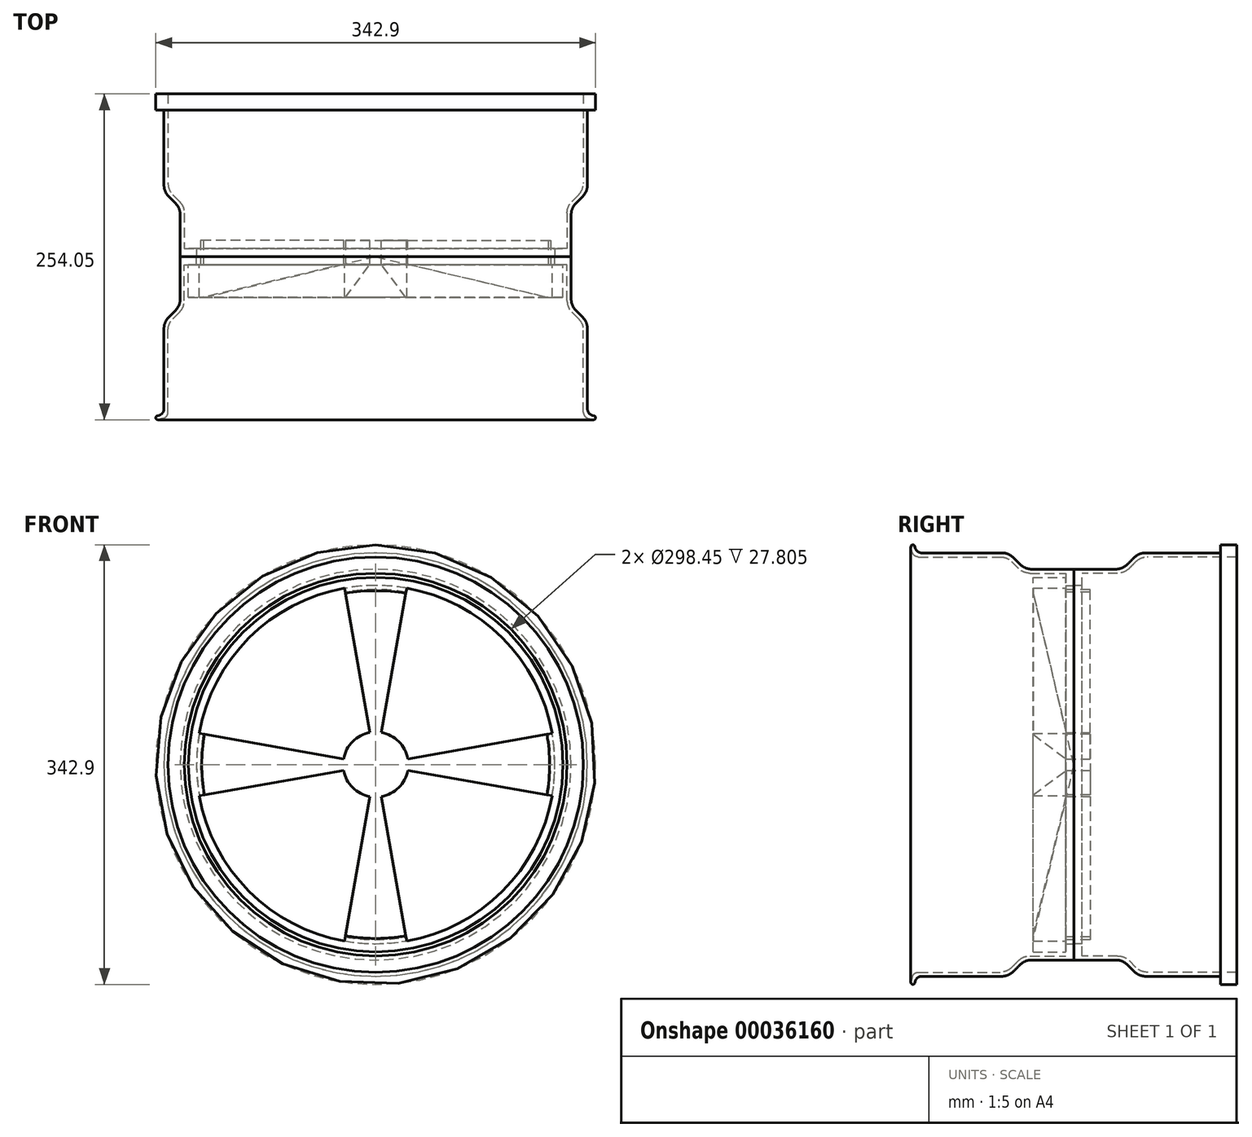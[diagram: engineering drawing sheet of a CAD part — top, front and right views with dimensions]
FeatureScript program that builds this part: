
annotation { "Feature Type Name" : "Feature", "Feature Type Description" : "" }
export const myFeature = defineFeature(function(context is Context, id is Id, definition is map)
    precondition{}
    {
        {
            var Q0;
            Q0=qCreatedBy(makeId("Right.planeOp"),FACE);
            var sketch = newSketch(context, id + "F0", { "sketchPlane" : qUnion([Q0])});
            skLineSegment(sketch, "E0", {"start": v(-127, 169.45) * mm, "end": v(-124.98, 161.93) * mm});
            skLineSegment(sketch, "E1", {"start": v(-39.42, 149.22) * mm, "end": v(-6.35, 149.22) * mm});
            skLineSegment(sketch, "E2", {"start": v(-6.35, 149.22) * mm, "end": v(-6.35, 139.7) * mm});
            skLineSegment(sketch, "E3", {"start": v(-6.35, 139.7) * mm, "end": v(0, 139.7) * mm});
            skLineSegment(sketch, "E4", {"start": v(0, 139.7) * mm, "end": v(0, 152.4) * mm});
            skLineSegment(sketch, "E5", {"start": v(0, 152.4) * mm, "end": v(-38.1, 152.4) * mm});
            skLineSegment(sketch, "E6", {"start": v(-122.55, 165.1) * mm, "end": v(-123.93, 170.27) * mm});
            skLineSegment(sketch, "E7", {"start": v(-38.1, 152.4) * mm, "end": v(-50.8, 165.1) * mm});
            skLineSegment(sketch, "E8", {"start": v(-50.8, 165.1) * mm, "end": v(-122.55, 165.1) * mm});
            skLineSegment(sketch, "E9", {"start": v(-39.42, 149.22) * mm, "end": v(-52.12, 161.92) * mm});
            skLineSegment(sketch, "E10", {"start": v(-52.12, 161.92) * mm, "end": v(-124.98, 161.92) * mm});
            skArc(sketch, "E11", {"start": v(-123.93, 170.27) * mm, "mid": v(-125.88, 171.4) * mm, "end": v(-127, 169.45) * mm});
            skLineSegment(sketch, "E12", {"start": v(-106.1, 171.45) * mm, "end": v(-79.8, 171.45) * mm, "construction": true});
            skLineSegment(sketch, "E13", {"start": v(0, 0) * mm, "end": v(-176.31, 0) * mm});
            skSolve(sketch);
        }
        {
            var Q0;
            Q0=makeQuery(id+"F0.imprint","IMPRINT",FACE,{"disambiguationData":[TD([[makeQuery(id+"F0.imprint","IMPRINT",EDGE,{"derivedFrom":sQuery(id+"F0.wireOp",EDGE,"E0")}),1.0]])]});
            var Q1;
            Q1=sQuery(id+"F0.wireOp",EDGE,"E13");
            revolve(context, id + "F1", {"entities" : qUnion([Q0]), "axis" : qUnion([Q1]), "revolveType" : RevolveType.FULL});
        }
        {
            var Q0;
            Q0=makeQuery(id+"F1.opRevolve","SWEPT_EDGE",EDGE,{"disambiguationData":[OSD([sQuery(id+"F0.wireOp",EDGE,"E7"),sQuery(id+"F0.wireOp",EDGE,"E8")])]});
            var Q1;
            Q1=makeQuery(id+"F1.opRevolve","SWEPT_EDGE",EDGE,{"disambiguationData":[OSD([sQuery(id+"F0.wireOp",EDGE,"E5"),sQuery(id+"F0.wireOp",EDGE,"E7")])]});
            var Q2;
            Q2=makeQuery(id+"F1.opRevolve","SWEPT_EDGE",EDGE,{"disambiguationData":[OSD([sQuery(id+"F0.wireOp",EDGE,"E1"),sQuery(id+"F0.wireOp",EDGE,"E9")])]});
            var Q3;
            Q3=makeQuery(id+"F1.opRevolve","SWEPT_EDGE",EDGE,{"disambiguationData":[OSD([sQuery(id+"F0.wireOp",EDGE,"E9"),sQuery(id+"F0.wireOp",EDGE,"E10")])]});
            fillet(context, id + "F2", {"entities" : qUnion([Q0, Q1, Q2, Q3]), "radius" : 12.7 * mm, "tangentPropagation" : true, "allowEdgeOverflow" : false});
        }
        {
            var Q0;
            Q0=makeQuery(id+"F1.opRevolve","SWEPT_EDGE",EDGE,{"disambiguationData":[OSD([sQuery(id+"F0.wireOp",EDGE,"E6"),sQuery(id+"F0.wireOp",EDGE,"E8")])]});
            var Q1;
            Q1=makeQuery(id+"F1.opRevolve","SWEPT_EDGE",EDGE,{"disambiguationData":[OSD([sQuery(id+"F0.wireOp",EDGE,"E0"),sQuery(id+"F0.wireOp",EDGE,"E10")])]});
            fillet(context, id + "F3", {"entities" : qUnion([Q0, Q1]), "radius" : 5.08 * mm, "tangentPropagation" : true, "allowEdgeOverflow" : false});
        }
        {
            var Q0;
            Q0=qCreatedBy(makeId("Right.planeOp"),FACE);
            var sketch = newSketch(context, id + "F4", { "sketchPlane" : qUnion([Q0])});
            skLineSegment(sketch, "E14", {"start": v(0, 139.7) * mm, "end": v(0, 152.4) * mm});
            skLineSegment(sketch, "E15", {"start": v(0, 152.4) * mm, "end": v(38.1, 152.4) * mm});
            skLineSegment(sketch, "E16", {"start": v(38.1, 152.4) * mm, "end": v(50.8, 165.1) * mm});
            skLineSegment(sketch, "E17", {"start": v(50.8, 165.1) * mm, "end": v(114.3, 165.1) * mm});
            skLineSegment(sketch, "E18", {"start": v(114.3, 165.1) * mm, "end": v(114.3, 171.45) * mm});
            skLineSegment(sketch, "E19", {"start": v(114.3, 171.45) * mm, "end": v(127, 171.45) * mm});
            skLineSegment(sketch, "E20", {"start": v(127, 171.45) * mm, "end": v(127, 161.93) * mm});
            skLineSegment(sketch, "E21", {"start": v(127, 161.93) * mm, "end": v(52.12, 161.93) * mm});
            skLineSegment(sketch, "E22", {"start": v(52.12, 161.93) * mm, "end": v(39.42, 149.23) * mm});
            skLineSegment(sketch, "E23", {"start": v(39.42, 149.23) * mm, "end": v(6.35, 149.23) * mm});
            skLineSegment(sketch, "E24", {"start": v(6.35, 149.23) * mm, "end": v(6.35, 139.7) * mm});
            skLineSegment(sketch, "E25", {"start": v(6.35, 139.7) * mm, "end": v(0, 139.7) * mm});
            skLineSegment(sketch, "E26", {"start": v(0, 0) * mm, "end": v(182.2, 0) * mm});
            skSolve(sketch);
        }
        {
            var Q0;
            Q0=makeQuery(id+"F4.imprint","IMPRINT",FACE,{"disambiguationData":[TD([[makeQuery(id+"F4.imprint","IMPRINT",EDGE,{"derivedFrom":sQuery(id+"F4.wireOp",EDGE,"E14")}),-1.0]])]});
            var Q1;
            Q1=sQuery(id+"F4.wireOp",EDGE,"E26");
            revolve(context, id + "F5", {"entities" : qUnion([Q0]), "axis" : qUnion([Q1]), "revolveType" : RevolveType.FULL});
        }
        {
            var Q0;
            Q0=makeQuery(id+"F5.opRevolve","SWEPT_EDGE",EDGE,{"disambiguationData":[OSD([sQuery(id+"F4.wireOp",EDGE,"E22"),sQuery(id+"F4.wireOp",EDGE,"E23")])]});
            var Q1;
            Q1=makeQuery(id+"F5.opRevolve","SWEPT_EDGE",EDGE,{"disambiguationData":[OSD([sQuery(id+"F4.wireOp",EDGE,"E21"),sQuery(id+"F4.wireOp",EDGE,"E22")])]});
            var Q2;
            Q2=makeQuery(id+"F5.opRevolve","SWEPT_EDGE",EDGE,{"disambiguationData":[OSD([sQuery(id+"F4.wireOp",EDGE,"E16"),sQuery(id+"F4.wireOp",EDGE,"E17")])]});
            var Q3;
            Q3=makeQuery(id+"F5.opRevolve","SWEPT_EDGE",EDGE,{"disambiguationData":[OSD([sQuery(id+"F4.wireOp",EDGE,"E15"),sQuery(id+"F4.wireOp",EDGE,"E16")])]});
            fillet(context, id + "F6", {"entities" : qUnion([Q0, Q1, Q2, Q3]), "radius" : 12.7 * mm, "tangentPropagation" : true, "allowEdgeOverflow" : false});
        }
        {
            var Q0;
            Q0=makeQuery(id+"F1.opRevolve","SWEPT_FACE",FACE,{"disambiguationData":[OSD([sQuery(id+"F0.wireOp",EDGE,"E2")])]});
            var sketch = newSketch(context, id + "F7", { "sketchPlane" : qUnion([Q0])});
            skCircle(sketch, "E27", {"center": v(0, 0) * mm, "radius": 146.05 * mm});
            skArc(sketch, "E28", {"start": v(-24.26, 137.58) * mm, "mid": v(-98.78, 98.78) * mm, "end": v(-137.58, 24.26) * mm});
            skCircle(sketch, "E29", {"center": v(0, 0) * mm, "radius": 50 * mm, "construction": true});
            skLineSegment(sketch, "E30", {"start": v(0, 0) * mm, "end": v(0, 139.7) * mm, "construction": true});
            skLineSegment(sketch, "E31", {"start": v(4.41, 25.01) * mm, "end": v(24.26, 137.58) * mm});
            skLineSegment(sketch, "E32", {"start": v(-4.41, 25.01) * mm, "end": v(-24.26, 137.58) * mm});
            skArc(sketch, "E33", {"start": v(-4.41, 25.01) * mm, "mid": v(-17.96, 17.96) * mm, "end": v(-25.01, 4.41) * mm});
            skLineSegment(sketch, "E34.1.0", {"start": v(-25.01, 4.41) * mm, "end": v(-137.58, 24.26) * mm});
            skLineSegment(sketch, "E34.1.1", {"start": v(-25.01, -4.41) * mm, "end": v(-137.58, -24.26) * mm});
            skLineSegment(sketch, "E34.2.0", {"start": v(-4.41, -25.01) * mm, "end": v(-24.26, -137.58) * mm});
            skLineSegment(sketch, "E34.2.1", {"start": v(4.41, -25.01) * mm, "end": v(24.26, -137.58) * mm});
            skLineSegment(sketch, "E35.1.3.0", {"start": v(25.01, -4.41) * mm, "end": v(137.58, -24.26) * mm});
            skLineSegment(sketch, "E35.3.3.0", {"start": v(25.01, 4.41) * mm, "end": v(137.58, 24.26) * mm});
            skArc(sketch, "E36.trimOffspring", {"start": v(137.58, 24.26) * mm, "mid": v(98.78, 98.78) * mm, "end": v(24.26, 137.58) * mm});
            skArc(sketch, "E37.trimOffspring", {"start": v(24.26, -137.58) * mm, "mid": v(98.78, -98.78) * mm, "end": v(137.58, -24.26) * mm});
            skArc(sketch, "E38.trimOffspring", {"start": v(-137.58, -24.26) * mm, "mid": v(-98.78, -98.78) * mm, "end": v(-24.26, -137.58) * mm});
            skArc(sketch, "E39.trimOffspring", {"start": v(-25.01, -4.41) * mm, "mid": v(-17.96, -17.96) * mm, "end": v(-4.41, -25.01) * mm});
            skArc(sketch, "E40.trimOffspring", {"start": v(4.41, -25.01) * mm, "mid": v(17.96, -17.96) * mm, "end": v(25.01, -4.41) * mm});
            skArc(sketch, "E41.trimOffspring", {"start": v(25.01, 4.41) * mm, "mid": v(17.96, 17.96) * mm, "end": v(4.41, 25.01) * mm});
            skSolve(sketch);
        }
        {
            var Q0;
            Q0=makeQuery(id+"F7.imprint","IMPRINT",FACE,{"disambiguationData":[TD([[makeQuery(id+"F7.imprint","IMPRINT",EDGE,{"derivedFrom":sQuery(id+"F7.wireOp",EDGE,"E27")}),1.0]])]});
            var Q1;
            {var subQ8=sQuery(id+"F7.wireOp",EDGE,"E31");Q1=makeQuery(id+"F7.imprint","IMPRINT",FACE,{"disambiguationData":[TD([[makeQuery(id+"F7.imprint","IMPRINT",EDGE,{"derivedFrom":subQ8}),1.0]])]});}
            extrude(context, id + "F8", {"entities" : qUnion([Q0, Q1]), "depth" : 25.4 * mm});
        }
        {
            var Q0;
            Q0=makeQuery(id+"F8.opExtrude","CAP_FACE",FACE,{"disambiguationData":[OSD([sQuery(id+"F7.wireOp",EDGE,"E27"),sQuery(id+"F7.wireOp",EDGE,"E28"),sQuery(id+"F7.wireOp",EDGE,"E31"),sQuery(id+"F7.wireOp",EDGE,"E32"),sQuery(id+"F7.wireOp",EDGE,"E33"),sQuery(id+"F7.wireOp",EDGE,"E34.1.0"),sQuery(id+"F7.wireOp",EDGE,"E34.1.1"),sQuery(id+"F7.wireOp",EDGE,"E34.2.0"),sQuery(id+"F7.wireOp",EDGE,"E34.2.1"),sQuery(id+"F7.wireOp",EDGE,"E35.1.3.0"),sQuery(id+"F7.wireOp",EDGE,"E35.3.3.0"),sQuery(id+"F7.wireOp",EDGE,"E36.trimOffspring"),sQuery(id+"F7.wireOp",EDGE,"E37.trimOffspring"),sQuery(id+"F7.wireOp",EDGE,"E38.trimOffspring"),sQuery(id+"F7.wireOp",EDGE,"E39.trimOffspring"),sQuery(id+"F7.wireOp",EDGE,"E40.trimOffspring"),sQuery(id+"F7.wireOp",EDGE,"E41.trimOffspring")])],"isStart":true});
            var sketch = newSketch(context, id + "F9", { "sketchPlane" : qUnion([Q0])});
            skArc(sketch, "E42", {"start": v(23.7, 134.45) * mm, "mid": v(0, 136.52) * mm, "end": v(-23.7, 134.45) * mm});
            skLineSegment(sketch, "E43", {"start": v(-23.7, 134.45) * mm, "end": v(-4.41, 25.01) * mm});
            skLineSegment(sketch, "E44", {"start": v(23.7, 134.45) * mm, "end": v(4.41, 25.01) * mm});
            skArc(sketch, "E45", {"start": v(-4.41, 25.01) * mm, "mid": v(-17.96, 17.96) * mm, "end": v(-25.01, 4.41) * mm});
            skLineSegment(sketch, "E46.1.0", {"start": v(-134.45, 23.7) * mm, "end": v(-25.01, 4.41) * mm});
            skLineSegment(sketch, "E46.1.1", {"start": v(-134.45, -23.7) * mm, "end": v(-25.01, -4.41) * mm});
            skArc(sketch, "E46.1.2", {"start": v(-134.45, 23.7) * mm, "mid": v(-136.52, 0) * mm, "end": v(-134.45, -23.7) * mm});
            skLineSegment(sketch, "E46.2.0", {"start": v(-23.7, -134.45) * mm, "end": v(-4.41, -25.01) * mm});
            skLineSegment(sketch, "E46.2.1", {"start": v(23.7, -134.45) * mm, "end": v(4.41, -25.01) * mm});
            skArc(sketch, "E46.2.2", {"start": v(-23.7, -134.45) * mm, "mid": v(0, -136.52) * mm, "end": v(23.7, -134.45) * mm});
            skLineSegment(sketch, "E46.3.0", {"start": v(134.45, -23.7) * mm, "end": v(25.01, -4.41) * mm});
            skLineSegment(sketch, "E46.3.1", {"start": v(134.45, 23.7) * mm, "end": v(25.01, 4.41) * mm});
            skArc(sketch, "E46.3.2", {"start": v(134.45, -23.7) * mm, "mid": v(136.52, 0) * mm, "end": v(134.45, 23.7) * mm});
            skArc(sketch, "E47.trimOffspring", {"start": v(-25.01, -4.41) * mm, "mid": v(-17.96, -17.96) * mm, "end": v(-4.41, -25.01) * mm});
            skArc(sketch, "E48.trimOffspring", {"start": v(4.41, -25.01) * mm, "mid": v(17.96, -17.96) * mm, "end": v(25.01, -4.41) * mm});
            skArc(sketch, "E49.trimOffspring", {"start": v(25.01, 4.41) * mm, "mid": v(17.96, 17.96) * mm, "end": v(4.41, 25.01) * mm});
            skSolve(sketch);
        }
        {
            var Q0;
            Q0=makeQuery(id+"F9.imprint","IMPRINT",FACE,{"disambiguationData":[TD([[makeQuery(id+"F9.imprint","IMPRINT",EDGE,{"derivedFrom":sQuery(id+"F9.wireOp",EDGE,"E42")}),1.0]])]});
            extrude(context, id + "F10", {"entities" : qUnion([Q0]), "operationType" : NewBodyOperationType.ADD, "depth" : 19.05 * mm});
        }
        {
            var Q0;
            Q0=qCreatedBy(makeId("Right.planeOp"),FACE);
            var sketch = newSketch(context, id + "F11", { "sketchPlane" : qUnion([Q0])});
            skLineSegment(sketch, "E50", {"start": v(0, 0) * mm, "end": v(-31.75, 0) * mm});
            skLineSegment(sketch, "E51", {"start": v(-31.75, 0) * mm, "end": v(-31.75, 135.59) * mm});
            skLineSegment(sketch, "E52", {"start": v(-31.75, 135.59) * mm, "end": v(0, 0) * mm});
            skSolve(sketch);
        }
        {
            var Q0;
            Q0 = qSketchRegion(id + "F11", true);
            var Q1;
            Q1=sQuery(id+"F11.wireOp",EDGE,"E50");
            revolve(context, id + "F12", {"operationType" : NewBodyOperationType.REMOVE, "entities" : qUnion([Q0]), "axis" : qUnion([Q1]), "revolveType" : RevolveType.FULL, "oppositeDirection" : true});
        }
    });
